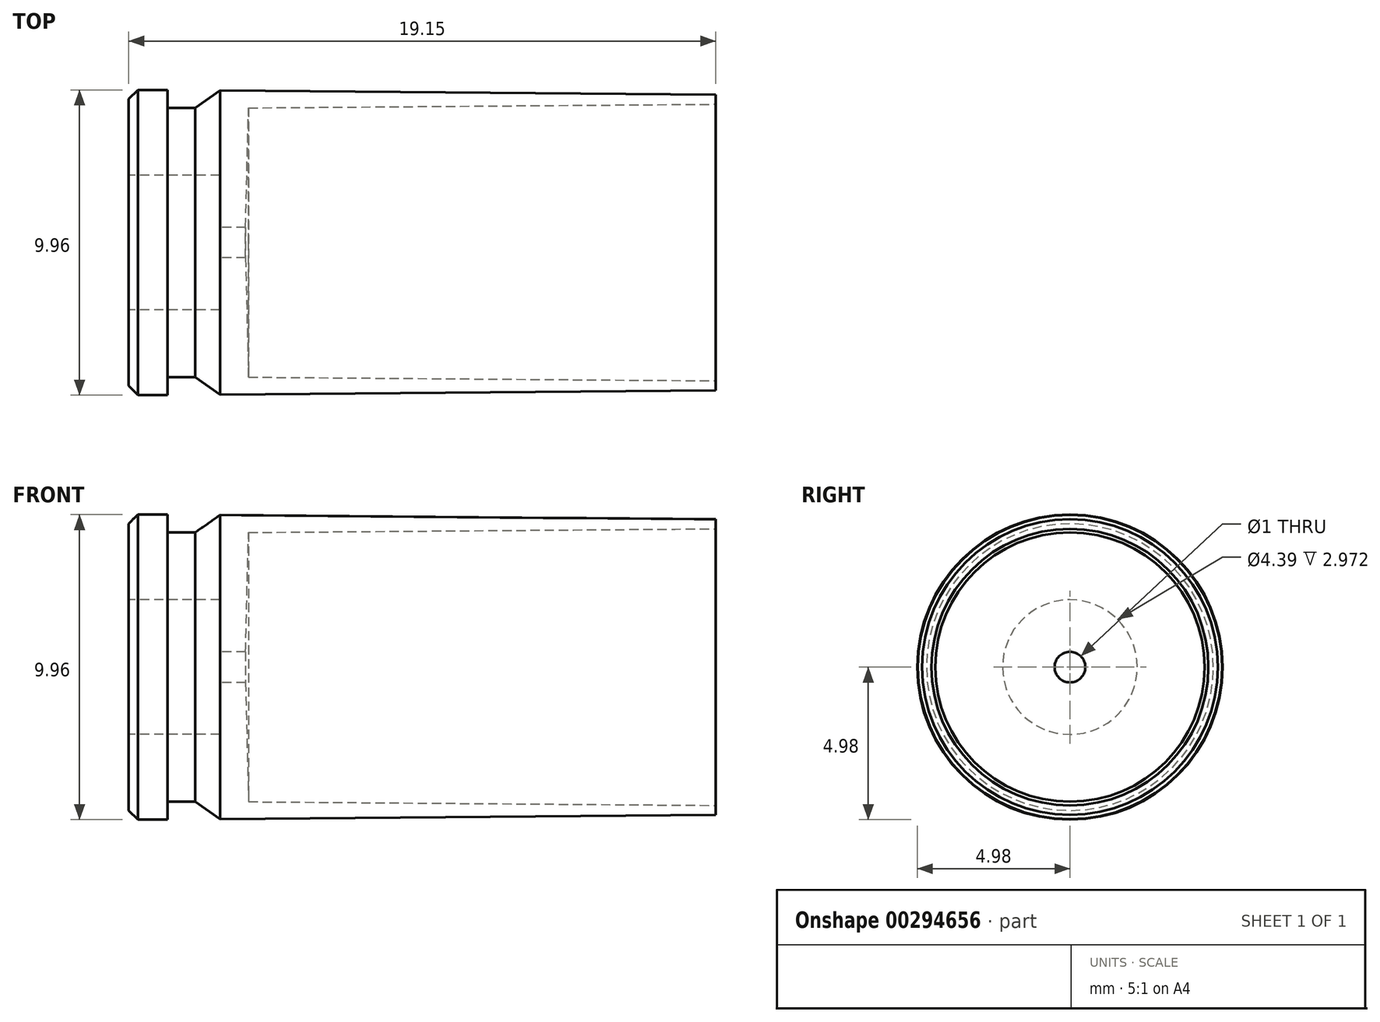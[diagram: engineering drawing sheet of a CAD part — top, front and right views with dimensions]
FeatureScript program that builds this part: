
annotation { "Feature Type Name" : "Feature", "Feature Type Description" : "" }
export const myFeature = defineFeature(function(context is Context, id is Id, definition is map)
    precondition{}
    {
        {
            var Q0;
            Q0=qCreatedBy(makeId("Front.planeOp"),FACE);
            var sketch = newSketch(context, id + "F0", { "sketchPlane" : qUnion([Q0])});
            skLineSegment(sketch, "E0", {"start": v(0, 0) * mm, "end": v(0, 4.68) * mm});
            skLineSegment(sketch, "E1", {"start": v(0, 4.68) * mm, "end": v(0.3, 4.98) * mm});
            skLineSegment(sketch, "E2", {"start": v(0.3, 4.98) * mm, "end": v(1.27, 4.98) * mm});
            skLineSegment(sketch, "E3", {"start": v(1.27, 4.98) * mm, "end": v(1.27, 4.4) * mm});
            skLineSegment(sketch, "E4", {"start": v(1.27, 4.4) * mm, "end": v(2.17, 4.4) * mm});
            skLineSegment(sketch, "E5", {"start": v(2.17, 4.4) * mm, "end": v(2.17, 4.4) * mm});
            skLineSegment(sketch, "E6", {"start": v(2.17, 4.4) * mm, "end": v(2.98, 4.96) * mm});
            skLineSegment(sketch, "E7", {"start": v(2.98, 4.96) * mm, "end": v(19.15, 4.83) * mm});
            skLineSegment(sketch, "E8", {"start": v(19.15, 4.83) * mm, "end": v(19.15, 4.51) * mm});
            skLineSegment(sketch, "E9", {"start": v(19.15, 4.51) * mm, "end": v(3.9, 4.4) * mm});
            skLineSegment(sketch, "E10", {"start": v(3.91, 4.4) * mm, "end": v(3.81, 0.5) * mm});
            skLineSegment(sketch, "E11", {"start": v(3.81, 0.5) * mm, "end": v(0, 0.5) * mm});
            skLineSegment(sketch, "E12", {"start": v(0, 0) * mm, "end": v(39.39, 0) * mm, "construction": true});
            skSolve(sketch);
        }
        {
            var Q0;
            {var subQ0=sQuery(id+"F0.wireOp",EDGE,"E1");Q0=makeQuery(id+"F0.imprint","IMPRINT",FACE,{"disambiguationData":[TD([[makeQuery(id+"F0.imprint","IMPRINT",EDGE,{"derivedFrom":subQ0}),-1.0]])]});}
            var Q1;
            Q1=sQuery(id+"F0.wireOp",EDGE,"E12");
            revolve(context, id + "F1", {"entities" : qUnion([Q0]), "axis" : qUnion([Q1]), "revolveType" : RevolveType.FULL});
        }
        {
            var Q0;
            Q0=makeQuery(id+"F1.opRevolve","SWEPT_FACE",FACE,{"disambiguationData":[OSD([sQuery(id+"F0.wireOp",EDGE,"E0")])]});
            var sketch = newSketch(context, id + "F2", { "sketchPlane" : qUnion([Q0])});
            skCircle(sketch, "E13", {"center": v(0, 0) * mm, "radius": 2.2 * mm});
            skSolve(sketch);
        }
        {
            var Q0;
            Q0=makeQuery(id+"F2.imprint","IMPRINT",FACE,{"disambiguationData":[TD([[makeQuery(id+"F2.imprint","IMPRINT",EDGE,{"derivedFrom":sQuery(id+"F2.wireOp",EDGE,"E13")}),1.0]])]});
            extrude(context, id + "F3", {"entities" : qUnion([Q0]), "operationType" : NewBodyOperationType.REMOVE, "oppositeDirection" : true, "depth" : 2.97 * mm});
        }
    });
